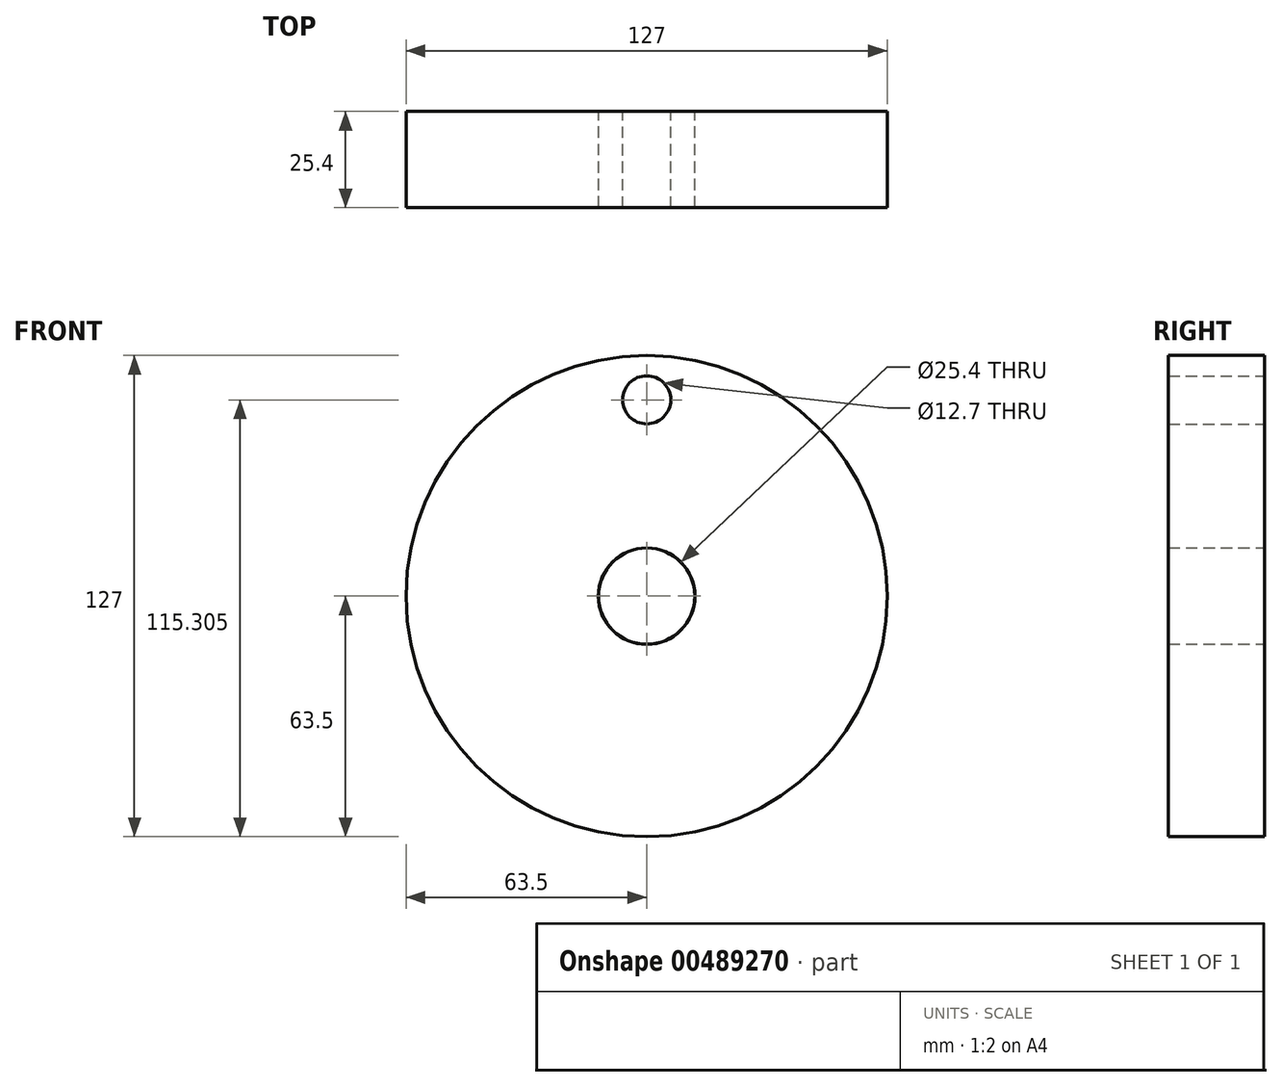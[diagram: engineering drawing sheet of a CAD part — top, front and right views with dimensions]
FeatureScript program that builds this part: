
annotation { "Feature Type Name" : "Feature", "Feature Type Description" : "" }
export const myFeature = defineFeature(function(context is Context, id is Id, definition is map)
    precondition{}
    {
        {
            var Q0;
            Q0=qCreatedBy(makeId("Front.planeOp"),FACE);
            var sketch = newSketch(context, id + "F0", { "sketchPlane" : qUnion([Q0])});
            skCircle(sketch, "E0", {"center": v(0, 0) * mm, "radius": 63.5 * mm});
            skCircle(sketch, "E1", {"center": v(0, 0) * mm, "radius": 12.7 * mm});
            skCircle(sketch, "E2", {"center": v(0, 51.8) * mm, "radius": 6.35 * mm});
            skSolve(sketch);
        }
        {
            var Q0;
            Q0=makeQuery(id+"F0.imprint","IMPRINT",FACE,{"disambiguationData":[TD([[makeQuery(id+"F0.imprint","IMPRINT",EDGE,{"derivedFrom":sQuery(id+"F0.wireOp",EDGE,"E0")}),1.0]])]});
            extrude(context, id + "F1", {"entities" : qUnion([Q0]), "depth" : 25.4 * mm});
        }
        {
            var Q0;
            Q0=makeQuery(id+"F1.opExtrude","SWEPT_FACE",FACE,{"disambiguationData":[OSD([sQuery(id+"F0.wireOp",EDGE,"E1")])]});
            chamfer(context, id + "F2", {"entities" : qUnion([Q0]), "width" : 0.05 * mm, "tangentPropagation" : true});
        }
    });
